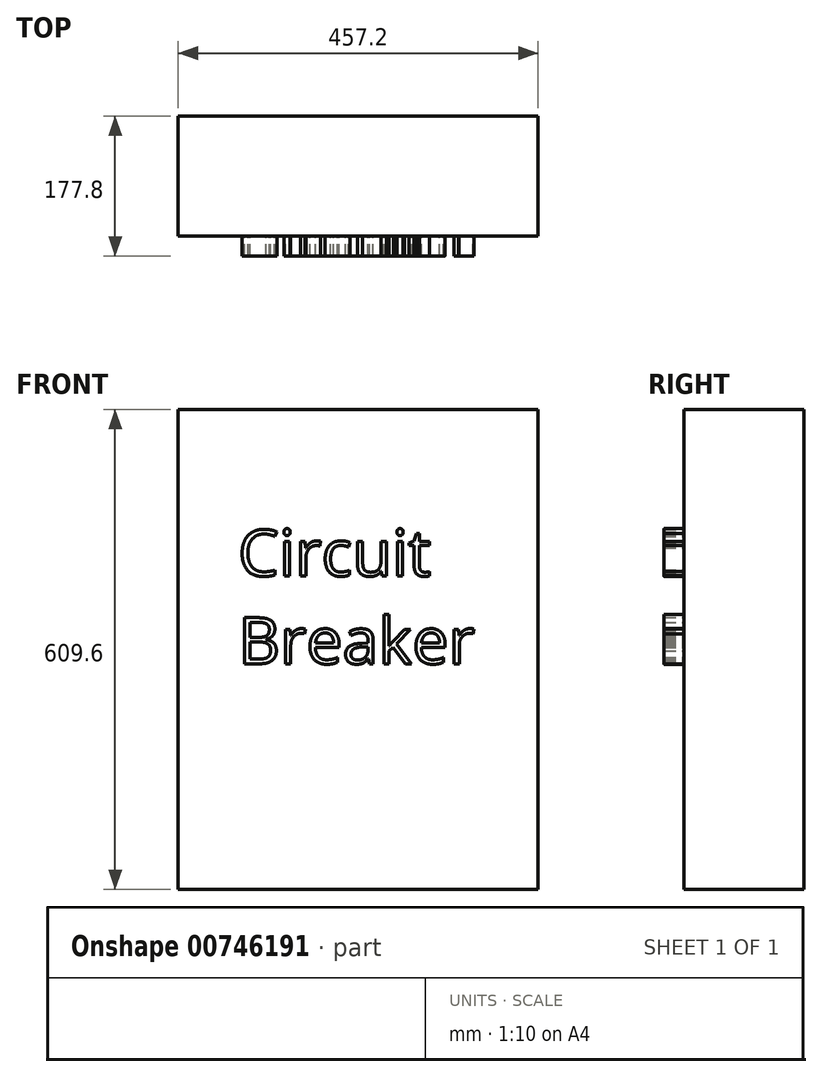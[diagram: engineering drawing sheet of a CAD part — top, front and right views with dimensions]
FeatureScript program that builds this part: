
annotation { "Feature Type Name" : "Feature", "Feature Type Description" : "" }
export const myFeature = defineFeature(function(context is Context, id is Id, definition is map)
    precondition{}
    {
        {
            var Q0;
            Q0=qCreatedBy(makeId("Front.planeOp"),FACE);
            var sketch = newSketch(context, id + "F0", { "sketchPlane" : qUnion([Q0])});
            skLineSegment(sketch, "E0.bottom", {"start": v(228.6, -304.8) * mm, "end": v(-228.6, -304.8) * mm});
            skLineSegment(sketch, "E0.top", {"start": v(228.6, 304.8) * mm, "end": v(-228.6, 304.8) * mm});
            skLineSegment(sketch, "E0.left", {"start": v(228.6, -304.8) * mm, "end": v(228.6, 304.8) * mm});
            skLineSegment(sketch, "E0.right", {"start": v(-228.6, -304.8) * mm, "end": v(-228.6, 304.8) * mm});
            skPoint(sketch, "E0.middle", {"position": v(0, 0) * mm});
            skSolve(sketch);
        }
        {
            var Q0;
            Q0=makeQuery(id+"F0.imprint","IMPRINT",FACE,{"disambiguationData":[TD([[makeQuery(id+"F0.imprint","IMPRINT",EDGE,{"derivedFrom":sQuery(id+"F0.wireOp",EDGE,"E0.bottom")}),-1.0]])]});
            extrude(context, id + "F1", {"entities" : qUnion([Q0]), "depth" : 152.4 * mm, "offsetDistance" : 30.48 * mm});
        }
        {
            var Q0;
            Q0=makeQuery(id+"F1.opExtrude","CAP_FACE",FACE,{"disambiguationData":[OSD([sQuery(id+"F0.wireOp",EDGE,"E0.bottom"),sQuery(id+"F0.wireOp",EDGE,"E0.top"),sQuery(id+"F0.wireOp",EDGE,"E0.left"),sQuery(id+"F0.wireOp",EDGE,"E0.right")])],"isStart":false});
            var sketch = newSketch(context, id + "F2", { "sketchPlane" : qUnion([Q0])});
            skText(sketch, "E1", { "text": "Circuit \nBreaker", "fontName": "OpenSans-Regular.ttf"});
            const initialGuessF2  = {"E1": [-0.1524, 0.09338, 1, 0, 0.05902]};
            skSetInitialGuess(sketch, initialGuessF2);
            skSolve(sketch);
        }
        {
            var Q0;
            Q0 = qSketchRegion(id + "F2", true);
            extrude(context, id + "F3", {"entities" : qUnion([Q0]), "operationType" : NewBodyOperationType.ADD, "depth" : 25.4 * mm, "offsetDistance" : 30.48 * mm});
        }
    });
